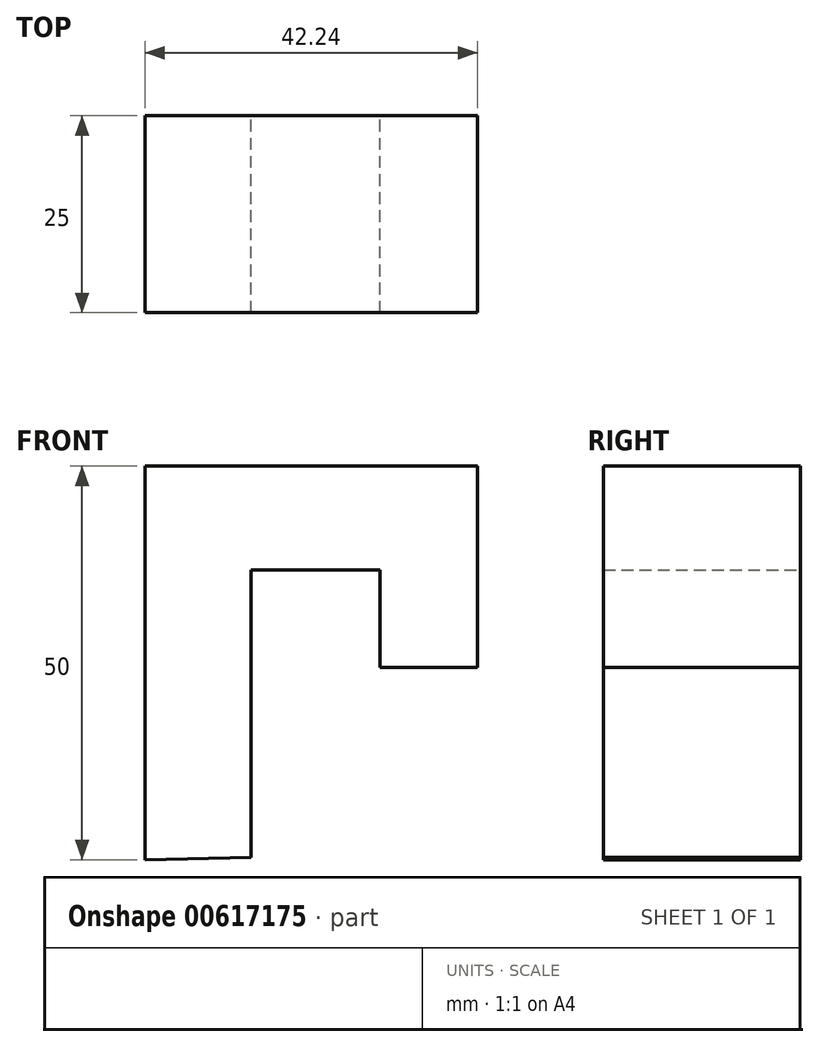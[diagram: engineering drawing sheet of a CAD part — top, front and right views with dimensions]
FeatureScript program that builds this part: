
annotation { "Feature Type Name" : "Feature", "Feature Type Description" : "" }
export const myFeature = defineFeature(function(context is Context, id is Id, definition is map)
    precondition{}
    {
        {
            var Q0;
            Q0=qCreatedBy(makeId("Front.planeOp"),FACE);
            var sketch = newSketch(context, id + "F0", { "sketchPlane" : qUnion([Q0])});
            skLineSegment(sketch, "E0", {"start": v(-54.42, 43) * mm, "end": v(-12.18, 43) * mm});
            skLineSegment(sketch, "E1", {"start": v(-54.42, 43) * mm, "end": v(-54.42, -7) * mm});
            skLineSegment(sketch, "E2", {"start": v(-12.18, 43) * mm, "end": v(-12.18, 17.43) * mm});
            skLineSegment(sketch, "E3", {"start": v(-12.18, 17.43) * mm, "end": v(-24.54, 17.43) * mm});
            skLineSegment(sketch, "E4", {"start": v(-24.54, 17.43) * mm, "end": v(-24.54, 29.78) * mm});
            skLineSegment(sketch, "E5", {"start": v(-24.54, 29.78) * mm, "end": v(-40.91, 29.78) * mm});
            skLineSegment(sketch, "E6", {"start": v(-40.91, 29.78) * mm, "end": v(-40.91, -6.71) * mm});
            skLineSegment(sketch, "E7", {"start": v(-54.42, -7) * mm, "end": v(-40.91, -6.71) * mm});
            skSolve(sketch);
        }
        {
            var Q0;
            Q0=makeQuery(id+"F0.imprint","IMPRINT",FACE,{"disambiguationData":[TD([[makeQuery(id+"F0.imprint","IMPRINT",EDGE,{"derivedFrom":sQuery(id+"F0.wireOp",EDGE,"E0")}),-1.0]])]});
            extrude(context, id + "F1", {"entities" : qUnion([Q0]), "depth" : 25 * mm, "offsetDistance" : 25 * mm});
        }
    });
